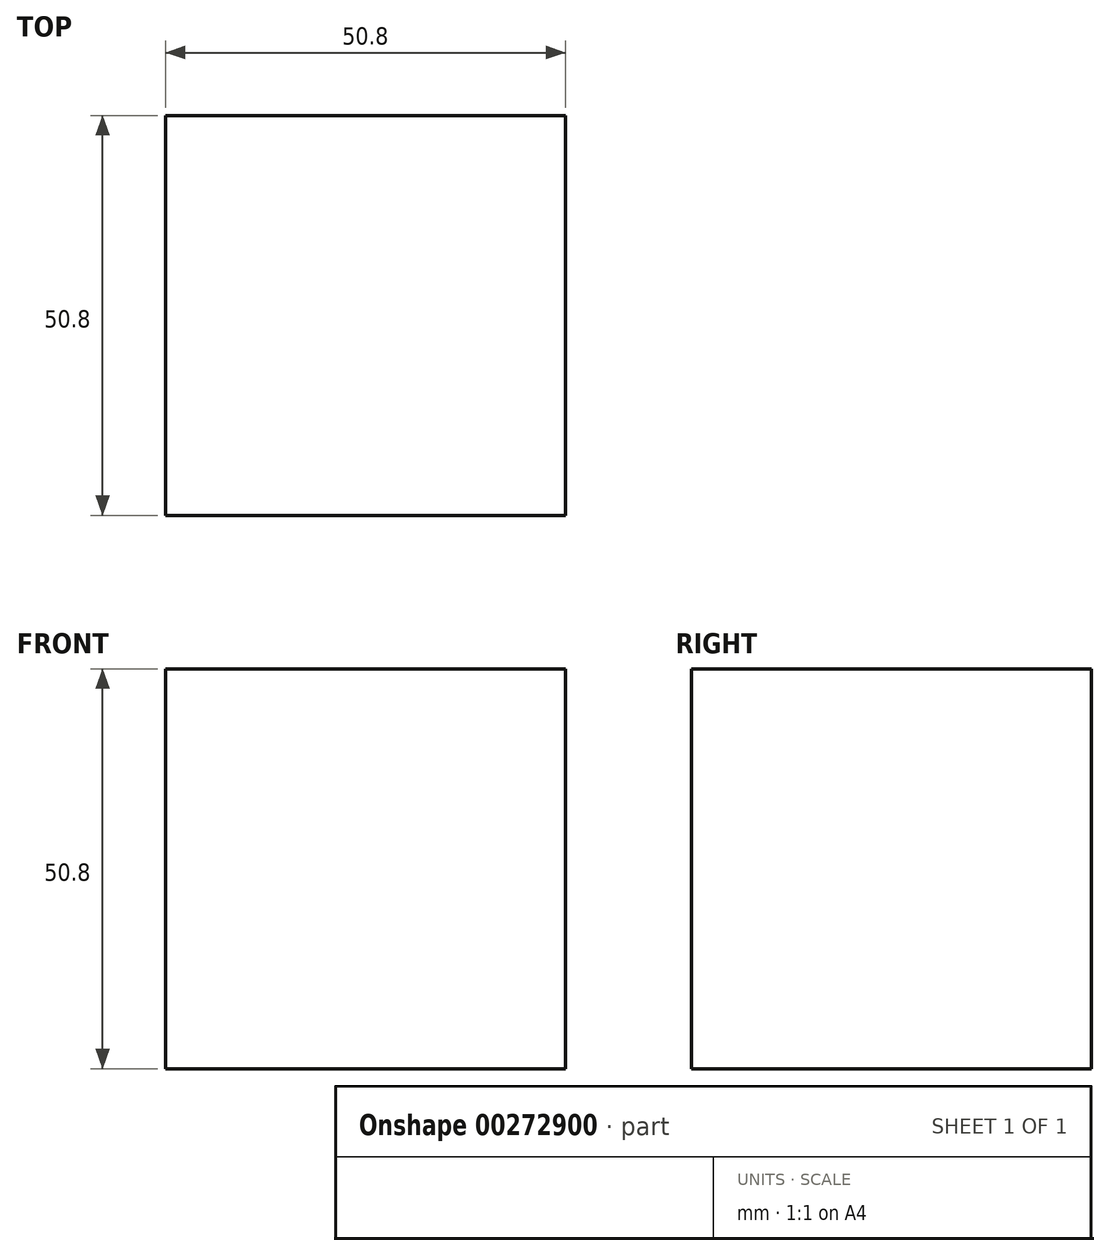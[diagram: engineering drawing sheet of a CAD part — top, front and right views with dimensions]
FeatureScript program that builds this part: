
annotation { "Feature Type Name" : "Feature", "Feature Type Description" : "" }
export const myFeature = defineFeature(function(context is Context, id is Id, definition is map)
    precondition{}
    {
        {
            var Q0;
            Q0=qCreatedBy(makeId("Front.planeOp"),FACE);
            var sketch = newSketch(context, id + "F0", { "sketchPlane" : qUnion([Q0])});
            skLineSegment(sketch, "E0", {"start": v(0, 0) * mm, "end": v(-50.8, 0) * mm});
            skLineSegment(sketch, "E1", {"start": v(-50.8, 50.8) * mm, "end": v(-50.8, 0) * mm});
            skLineSegment(sketch, "E2", {"start": v(-50.8, 50.8) * mm, "end": v(0, 50.8) * mm});
            skLineSegment(sketch, "E3", {"start": v(0, 50.8) * mm, "end": v(0, 0) * mm});
            skSolve(sketch);
        }
        {
            var Q0;
            Q0 = qSketchRegion(id + "F0", true);
            extrude(context, id + "F1", {"entities" : qUnion([Q0]), "depth" : 50.8 * mm});
        }
    });
